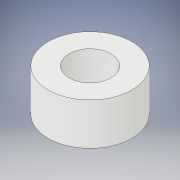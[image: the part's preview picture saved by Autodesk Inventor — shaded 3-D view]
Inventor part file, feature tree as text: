
AUTODESK INVENTOR PART (.ipt)
format: ipt  version: 2018 (Build 220112000, 112)  size: 107,008 bytes
history: native  units: in
note: dims shown in document units (in); Inventor stores cm internally (conversion verified against a paired STEP export)
features: extrude x1, sketch x1
ambient origin geometry x8: Origin, YZ Plane, XZ Plane, XY Plane, X Axis, Y Axis, Z Axis, Center Point
bodies: Solid1 (feature_tree)
feature tree (2):
  extrude  "Extrusion1"  Depth=0.1181in
  sketch  "Sketch1"  dims[d0=0.1181in d1=0.2362in d2=0.1181in d3=0.0in]
